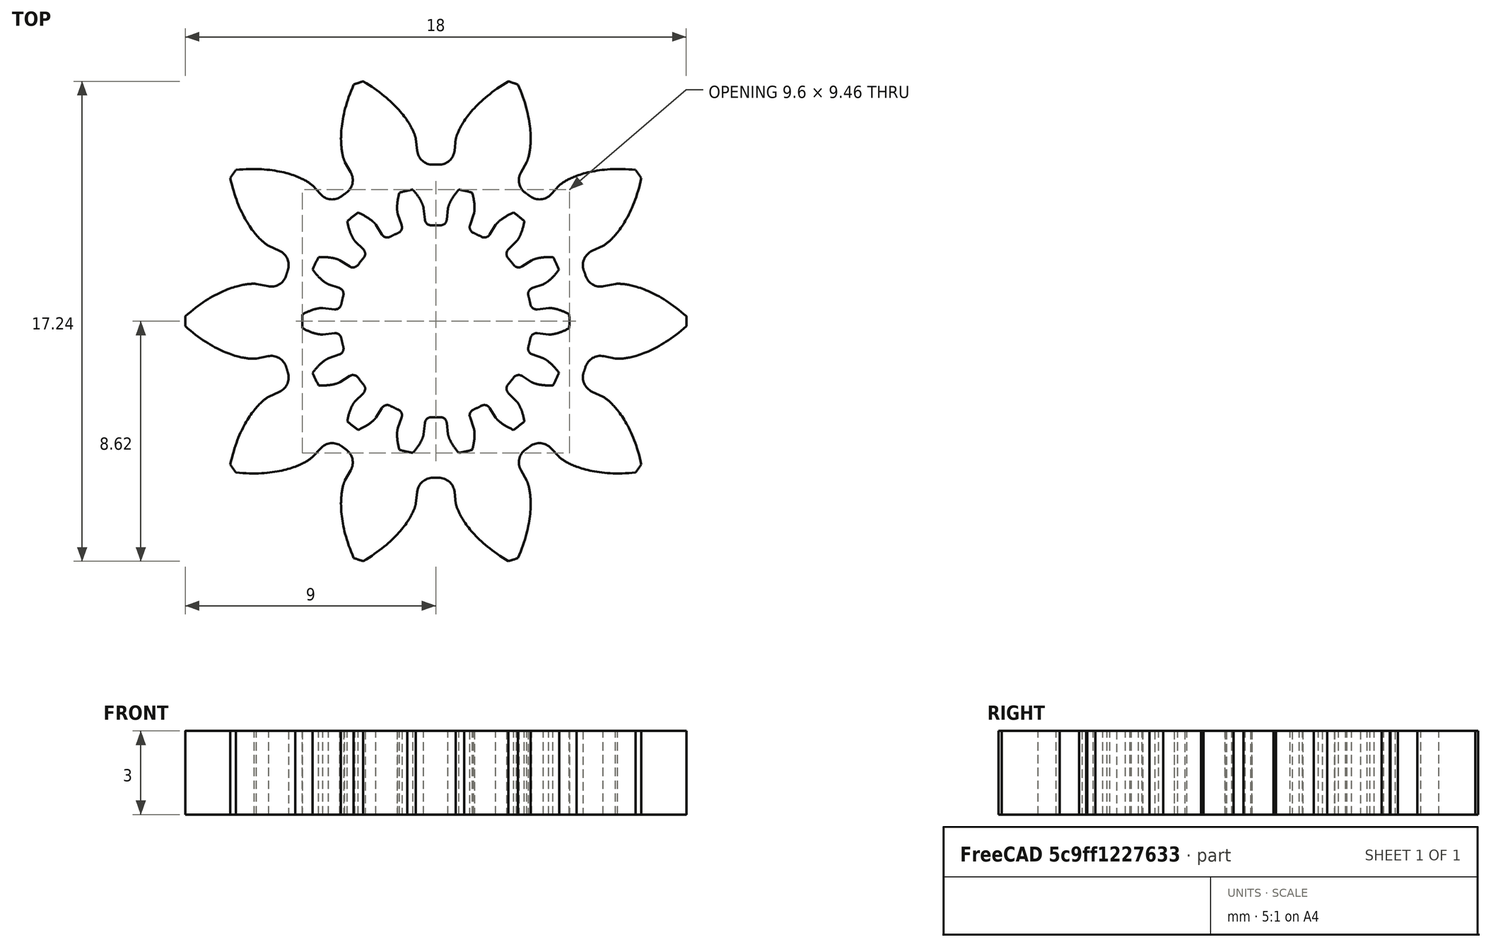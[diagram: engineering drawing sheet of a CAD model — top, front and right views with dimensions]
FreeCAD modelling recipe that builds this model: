
FCSTD DOCUMENT  (FreeCAD 0.14R3702 (Git))
Label: rueda-dentada-pequena
License: CC-BY 3.0
LicenseURL: http://creativecommons.org/licenses/by/3.0/
objects: Part::Part2DObjectPython×2, Part::Extrusion×2, Part::Cut×1
note: 5 computed .brp shape members not serialized (recipe doc carries the construction recipe); baked Part::Feature solids carry a one-line shape summary decoded from their .brp

FEATURE [Part::Part2DObjectPython] InvoluteGear  label="rueda-exterior"  # Draft 2D object (typed FeaturePython)
  Modules = 1.5
  NumberOfCurves = 0
  NumberOfTeeth = 10
  PressureAngle = 29
FEATURE [Part::Part2DObjectPython] InvoluteGear001  label="rueda-interior"  # Draft 2D object (typed FeaturePython)
  Modules = 0.6
  NumberOfCurves = 0
  NumberOfTeeth = 14
  PressureAngle = 14
FEATURE [Part::Extrusion] Extrude
  Base = -> InvoluteGear
  Dir = (0,0,3)
  Solid = true
FEATURE [Part::Extrusion] Extrude001
  Base = -> InvoluteGear001
  Dir = (0,0,3)
  Solid = true
FEATURE [Part::Cut] Cut  label="rueda-dentada-pequena"
  Base = -> Extrude
  Tool = -> Extrude001
